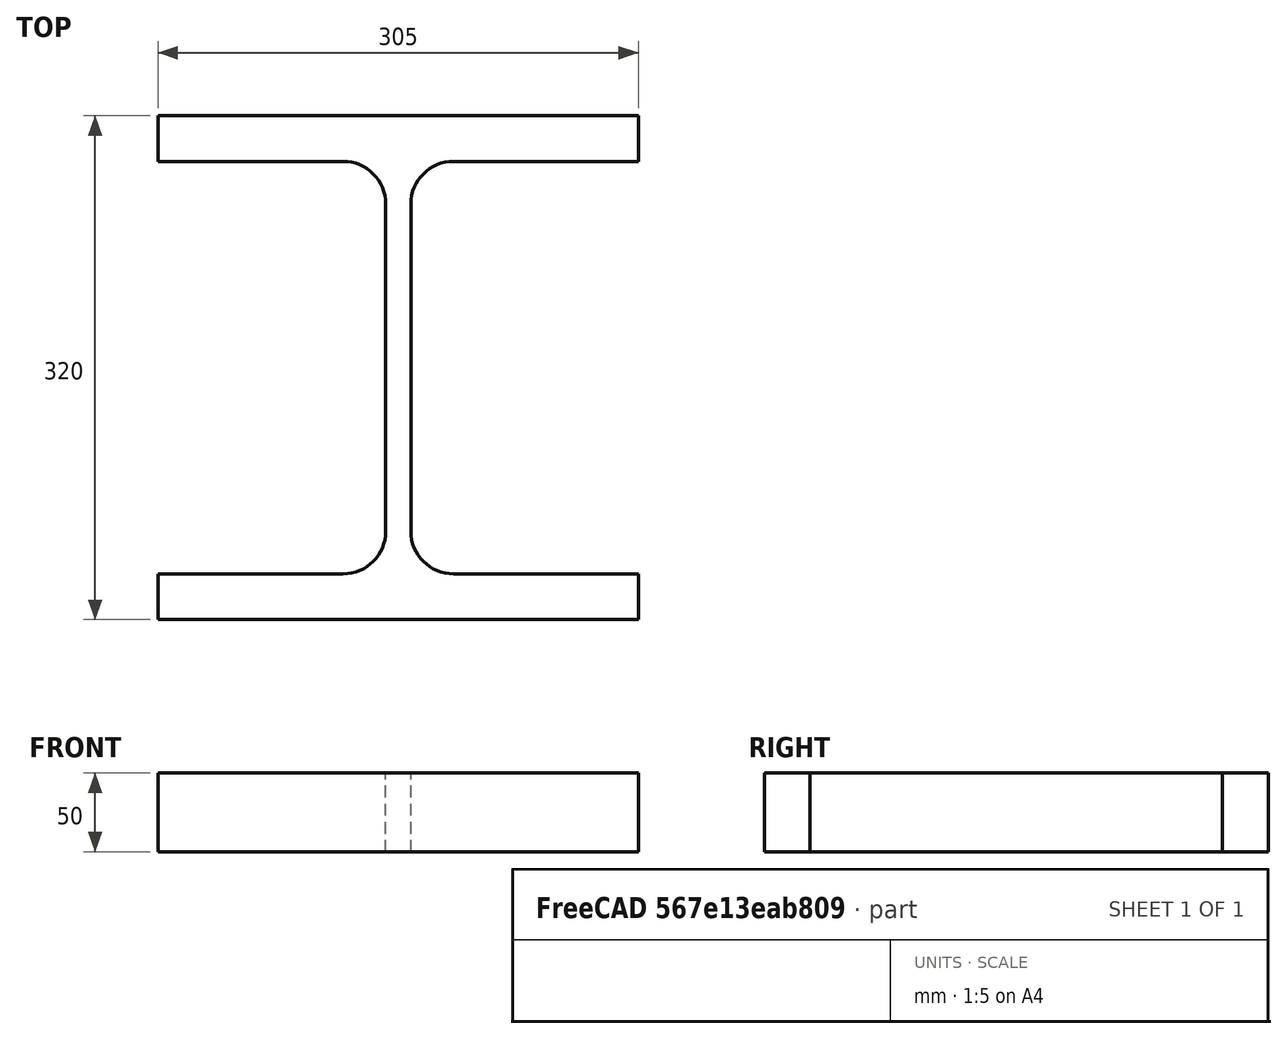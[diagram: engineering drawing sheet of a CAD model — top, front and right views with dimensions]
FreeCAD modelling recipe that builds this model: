
FCSTD DOCUMENT  (FreeCAD 0.15R4671 (Git))
Label: HE-M-Profile 320x305 DIN1025-4 S235JR
License: All rights reserved
LicenseURL: http://en.wikipedia.org/wiki/All_rights_reserved
objects: Sketcher::SketchObject×1, Part::Extrusion×1
note: 2 computed .brp shape members not serialized (recipe doc carries the construction recipe); baked Part::Feature solids carry a one-line shape summary decoded from their .brp

FEATURE [Sketcher::SketchObject] Sketch
  sketch-geometry (16):
    g0: LineSegment StartX=8 StartY=-104 StartZ=0 EndX=8 EndY=104 EndZ=0
    g1: LineSegment StartX=35 StartY=131 StartZ=0 EndX=152.5 EndY=131 EndZ=0
    g2: LineSegment StartX=152.5 StartY=131 StartZ=0 EndX=152.5 EndY=160 EndZ=0
    g3: LineSegment StartX=152.5 StartY=160 StartZ=0 EndX=-152.5 EndY=160 EndZ=0
    g4: LineSegment StartX=-152.5 StartY=160 StartZ=0 EndX=-152.5 EndY=131 EndZ=0
    g5: LineSegment StartX=-152.5 StartY=131 StartZ=0 EndX=-35 EndY=131 EndZ=0
    g6: LineSegment StartX=-8 StartY=104 StartZ=0 EndX=-8 EndY=-104 EndZ=0
    g7: LineSegment StartX=-35 StartY=-131 StartZ=0 EndX=-152.5 EndY=-131 EndZ=0
    g8: LineSegment StartX=-152.5 StartY=-131 StartZ=0 EndX=-152.5 EndY=-160 EndZ=0
    g9: LineSegment StartX=-152.5 StartY=-160 StartZ=0 EndX=152.5 EndY=-160 EndZ=0
    g10: LineSegment StartX=152.5 StartY=-160 StartZ=0 EndX=152.5 EndY=-131 EndZ=0
    g11: LineSegment StartX=152.5 StartY=-131 StartZ=0 EndX=35 EndY=-131 EndZ=0
    g12: ArcOfCircle CenterX=35 CenterY=104 CenterZ=0 NormalX=0 NormalY=0 NormalZ=1 Radius=27 StartAngle=1.5708 EndAngle=3.14159
    g13: ArcOfCircle CenterX=35 CenterY=-104 CenterZ=0 NormalX=0 NormalY=0 NormalZ=1 Radius=27 StartAngle=3.14159 EndAngle=4.71239
    g14: ArcOfCircle CenterX=-35 CenterY=104 CenterZ=0 NormalX=0 NormalY=0 NormalZ=1 Radius=27 StartAngle=0 EndAngle=1.5708
    g15: ArcOfCircle CenterX=-35 CenterY=-104 CenterZ=0 NormalX=0 NormalY=0 NormalZ=1 Radius=27 StartAngle=4.71239 EndAngle=6.28319
  constraints (42):
    c: Vertical(g0)
    c: Coincident(g2,g1)
    c: Vertical(g2)
    c: Coincident(g3,g2)
    c: Coincident(g4,g3)
    c: Vertical(g4)
    c: Coincident(g5,g4)
    c: Horizontal(g5)
    c: Vertical(g6)
    c: Horizontal(g7)
    c: Coincident(g8,g7)
    c: Vertical(g8)
    c: Coincident(g9,g8)
    c: Horizontal(g9)
    c: Coincident(g10,g9)
    c: Vertical(g10)
    c: Coincident(g11,g10)
    c: Horizontal(g11)
    c: Tangent(g1,g12) = 1.5708
    c: Tangent(g0,g12) = 1.5708
    c: Tangent(g0,g13) = 1.5708
    c: Tangent(g11,g13) = 1.5708
    c: Tangent(g5,g14) = 1.5708
    c: Tangent(g6,g14) = 1.5708
    c: Tangent(g6,g15) = 1.5708
    c: Tangent(g7,g15) = 1.5708
    c: Equal(g3,g9)
    c: Equal(g2,g4)
    c: Equal(g4,g8)
    c: Equal(g8,g10)
    c: Equal(g12,g14)
    c: Equal(g14,g15)
    c: Equal(g15,g13)
    c: Symmetric(g2,g3,g-2)
    c: Symmetric(g9,g8,g-2)
    c: Symmetric(g0,g6,g-2)
    c: Symmetric(g2,g9,g-1)
    c: DistanceY(g2,g9) = -320
    c: DistanceX(g3) = -305
    c: DistanceX(g0,g6) = -16
    c: DistanceY(g2) = 29
    c: Radius(g12) = 27
FEATURE [Part::Extrusion] Extrude  label="HE-M-Profile 320x305 DIN1025-4 S235JR"
  Base = -> Sketch
  Dir = (0,0,50)
  Solid = true
